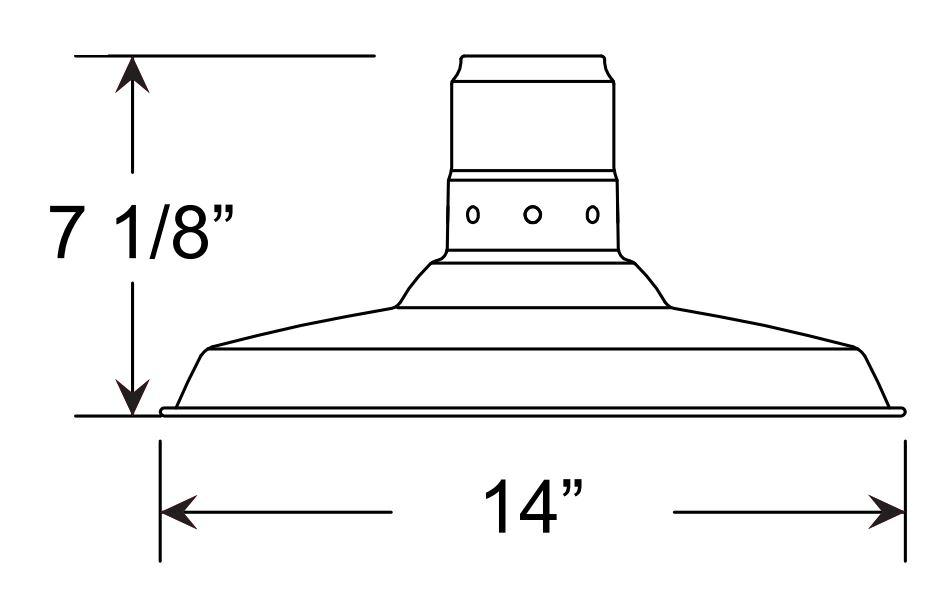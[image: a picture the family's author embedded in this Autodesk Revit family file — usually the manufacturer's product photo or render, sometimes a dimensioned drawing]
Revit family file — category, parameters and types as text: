
# Revit family: SPO-KEY-BP MB
name_source: partatom
category: Lighting Fixtures
units: mm (PartAtom-declared; Revit-internal decimal feet)

## family parameters
Always vertical = Yes
Cut with Voids When Loaded = No
Light Source = Yes
OmniClass Number = 23.80.70.00
OmniClass Title = Lighting
Part Type = Normal
Room Calculation Point = No
Round Connector Dimension = Use Diameter
Shared = No
Work Plane-Based = No

## types (1)
- SPO-KEY-BP
    Apparent Load = 60 VA
    Body Colour = Spun aluminium
    Body Material = body
    Color Filter = 16777215
    Construction Material = Heavy Duty spun aluminum.
    Default Elevation = 0' - 0"
    Description = 120-277 Voltage
    Dimming Lamp Color Temperature Shift = <None>
    Fixture Diameter = 0' - 1 1/2"
    Fixture Height = 0' - 3 1/2"
    GLASS = Glass
    Lamp = MED-BASE
    Load Classification = Lighting
    Manufacturer = ANP Lighting
    Model = SPO-KEY-BP
    Photometric Web File = generic.ies
    Power Factor = 1
    Ring = RING
    SPO-KEY-BP = Yes
    Tilt Angle = 90.00°
    URL = https://www.anplighting.com
    Voltage = 277 V
    Warranty = 5 year limited warranty
    Wattage Comments = 60W Max
    Weight = 0.30 lbs

## geometry (parser evidence)
native form markers: Sweep x21
no freeform markers — native parametric forms only
